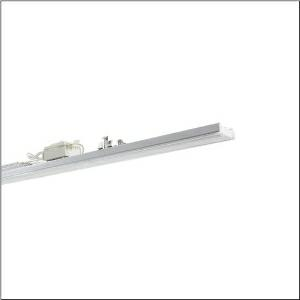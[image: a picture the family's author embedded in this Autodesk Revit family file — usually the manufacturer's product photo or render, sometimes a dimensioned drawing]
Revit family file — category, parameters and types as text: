
# Revit family: licross_21_recessed_mo_52tl14dn49xg
name_source: partatom
category: Lighting Fixtures
units: mm (PartAtom-declared; Revit-internal decimal feet)

## family parameters
Cut with Voids When Loaded = No
Host = Face
Light Source = No
Part Type = Normal
Room Calculation Point = No
Round Connector Dimension = Use Diameter
Shared = No

## types (1)
- --- (1 x LED, 9470 lm, 58 W, 4000K)
    Apparent Load = 58 VA
    CIE Flux Codes = 56 84 97 100 100
    Color Rendering = 80
    Color Temperature = 4000K
    Default Elevation = 1800 mm
    Description = Licross 21 Recessed MO, luminaire insert, of sheet steel, galvanised, coil coated, white, length: 1.500mm, width: 66mm, height: 67mm, LED rated luminous flux: 9.470lm, light colour: 840, SDCM (Standard Deviation of Colour Matching)MacAdam ≤ 3 SDCM (initial), control gear: DALI 2, with plug, 5-pole, with phase selection, mains connection: 220..240V, AC, 50/60Hz, rated input power: 58W, internal wiring halogen-free, primary light control with lens, of plastic, primary optical cover: cover, of PMMA, light emission: direct distribution, primary light characteristic: asymmetric, protection rating (complete): IP40, insulation class (complete): insulation class I (protective earthing), certification: CE, ENEC, VDE, UKCA, protection symbol: D if used in an environment without relevant dust loads with corresponding accessories, impact resistance: IK06, permissible ambient temperature for indoor applications: -25..+35°C, corresponds to IFS (International Featured Standards) requirements for safety and quality in the food industry, reducing of maximum allowable ambient temperature of 5°C with ceiling mounting, LABS conformity tested according to VDMA 24364:2018-05, The light source and the operating device comply with the requirements of the Ecodesign Regulation (EU) 2019/2020 and are replaceable in accordance with this regulation, packaging unit: 1 piece
    Height = 58 mm
    Lamp = 1 x LED
    Lamp Light Flux = 9470 lm
    Lamp Power = 58 W
    Lamp count = 1
    Length = 1500 mm
    Luminous efficacy = 163 lm/W
    Manufacturer = Siteco
    ModVariant = No
    Model = 52TL14DN49XG
    Mounting Place = Ceiling
    Mounting Type = Pendant
    Number of Poles = 1
    OnlyDefault = Yes
    Power Factor = 1
    Product Name = Licross 21 Recessed MO
    Product group = luminaire insert | ceiling pendant
    ProductGroupID = 901
    Protection Class = Protection class I
    Protection Degree = IP 40
    RLX_Detail_Level = 1
    RLX_Emergency_Light_Flux = 0 lm
    RLX_Emergency_Type = 0
    RLX_Emergency_Type_DB = No
    RlxData = <blob elided: 25265 chars, md5=5943f230>
    Socket = socket
    Standby Power = 0 W
    System Light Flux = 9470 lm
    System Power = 58 W
    Type Comments = factory setting: luminous flux: 100 % | dim-lin: 254 | 390 mA
    Type Image = l_1296930.jpg
    URL = http://relux.com
    VarID = @adj_127925
    Voltage = 0 V
    Weight = 0.00 kg
    Width = 66 mm

## geometry (parser evidence)
native form markers: Blend x4, Sweep x11
no freeform markers — native parametric forms only
